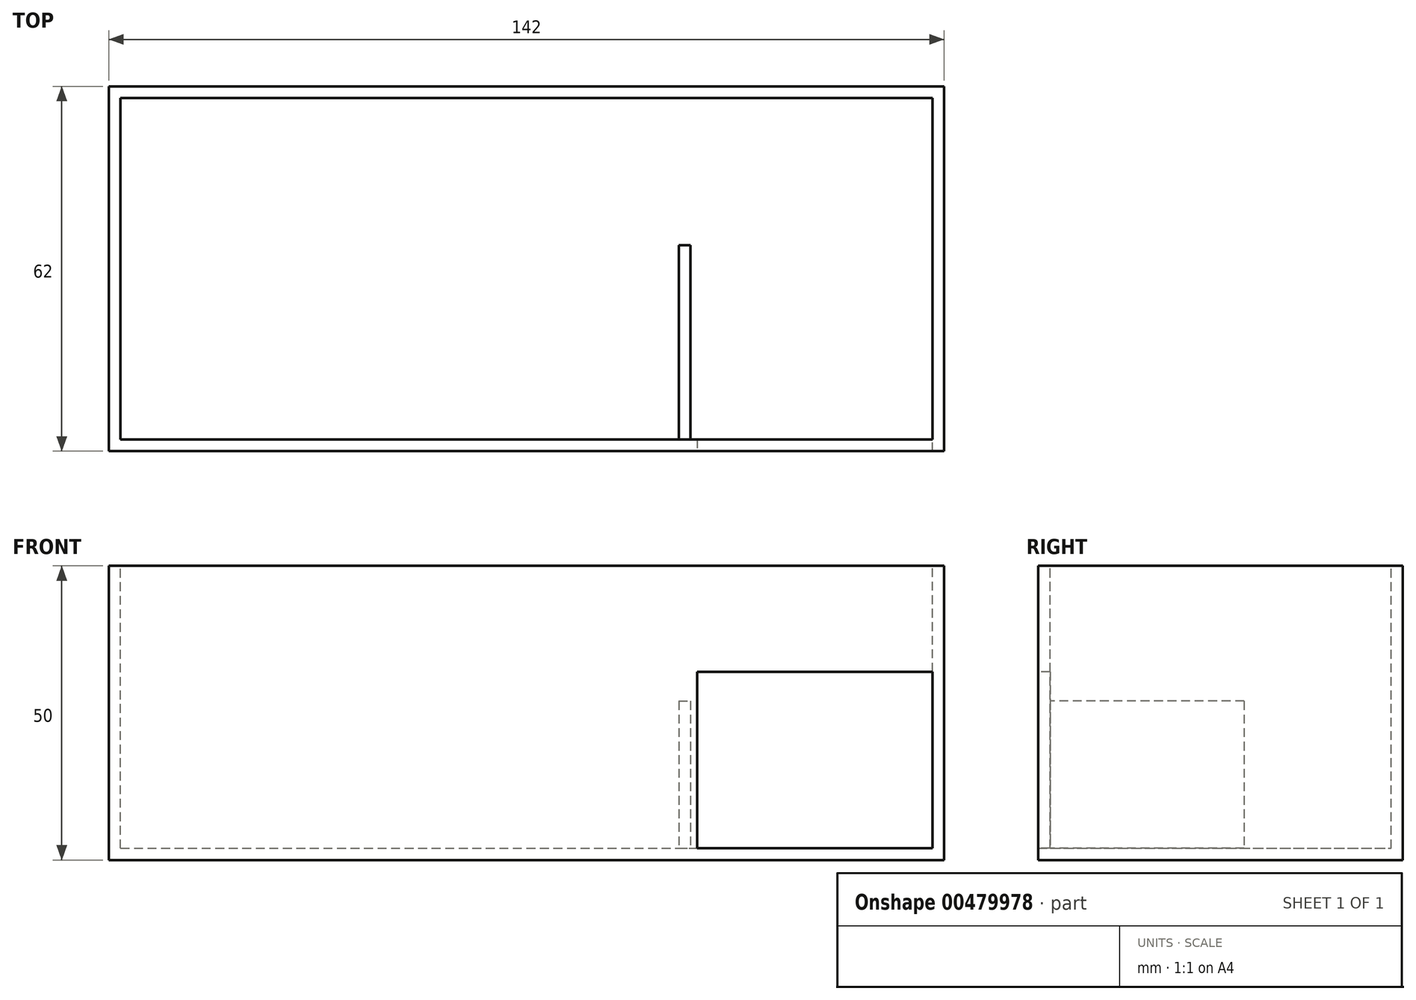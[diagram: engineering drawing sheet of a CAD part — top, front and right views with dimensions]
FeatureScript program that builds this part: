
annotation { "Feature Type Name" : "Feature", "Feature Type Description" : "" }
export const myFeature = defineFeature(function(context is Context, id is Id, definition is map)
    precondition{}
    {
        {
            var Q0;
            Q0=qCreatedBy(makeId("Top.planeOp"),FACE);
            var sketch = newSketch(context, id + "F0", { "sketchPlane" : qUnion([Q0])});
            skLineSegment(sketch, "E0.bottom", {"start": v(-36.08, 27.4) * mm, "end": v(105.92, 27.4) * mm});
            skLineSegment(sketch, "E0.top", {"start": v(-36.08, -34.6) * mm, "end": v(105.92, -34.6) * mm});
            skLineSegment(sketch, "E0.left", {"start": v(-36.08, 27.4) * mm, "end": v(-36.08, -34.6) * mm});
            skLineSegment(sketch, "E0.right", {"start": v(105.92, 27.4) * mm, "end": v(105.92, -34.6) * mm});
            skSolve(sketch);
        }
        {
            var Q0;
            Q0 = qSketchRegion(id + "F0", true);
            var Q1;
            Q1 = qSketchRegion(id + "F5", true);
            extrude(context, id + "F1", {"entities" : qUnion([Q0, Q1]), "depth" : 50 * mm});
        }
        {
            var Q0;
            Q0=makeQuery(id+"F1.opExtrude","CAP_FACE",FACE,{"disambiguationData":[OSD([sQuery(id+"F0.wireOp",EDGE,"E0.bottom"),sQuery(id+"F0.wireOp",EDGE,"E0.top"),sQuery(id+"F0.wireOp",EDGE,"E0.left"),sQuery(id+"F0.wireOp",EDGE,"E0.right")])],"isStart":false});
            var sketch = newSketch(context, id + "F2", { "sketchPlane" : qUnion([Q0])});
            skLineSegment(sketch, "E1.bottom", {"start": v(-34.08, 25.4) * mm, "end": v(103.92, 25.4) * mm});
            skLineSegment(sketch, "E1.top", {"start": v(-34.08, -32.6) * mm, "end": v(103.92, -32.6) * mm});
            skLineSegment(sketch, "E1.left", {"start": v(-34.08, -32.6) * mm, "end": v(-34.08, 25.4) * mm});
            skLineSegment(sketch, "E1.right", {"start": v(103.92, -32.6) * mm, "end": v(103.92, 25.4) * mm});
            skSolve(sketch);
        }
        {
            var Q0;
            Q0 = qSketchRegion(id + "F2", true);
            extrude(context, id + "F3", {"entities" : qUnion([Q0]), "operationType" : NewBodyOperationType.REMOVE, "oppositeDirection" : true, "depth" : 48 * mm});
        }
        {
            var Q0;
            Q0=makeQuery(id+"F3.boolean.opBoolean","COPY",FACE,{"derivedFrom":makeQuery(id+"F3.opExtrude","CAP_FACE",FACE,{"disambiguationData":[OSD([sQuery(id+"F2.wireOp",EDGE,"E1.bottom"),sQuery(id+"F2.wireOp",EDGE,"E1.top"),sQuery(id+"F2.wireOp",EDGE,"E1.left"),sQuery(id+"F2.wireOp",EDGE,"E1.right")])],"isStart":false})});
            var sketch = newSketch(context, id + "F4", { "sketchPlane" : qUnion([Q0])});
            skLineSegment(sketch, "E2", {"start": v(55.92, 25.4) * mm, "end": v(55.92, -32.6) * mm});
            skPoint(sketch, "E2.endSnap0", {"position": v(34.92, -32.6) * mm});
            skSolve(sketch);
        }
        {
            var Q0;
            {var subQ0=sQuery(id+"F2.wireOp",EDGE,"E1.bottom");var subQ1=sQuery(id+"F2.wireOp",EDGE,"E1.top");var subQ2=sQuery(id+"F2.wireOp",EDGE,"E1.left");Q0=makeQuery(id+"FYpbpyhjp7itbWw_2.boolean.opBoolean","SPLIT",FACE,{"disambiguationData":[TD([makeQuery(id+"F3.boolean.opBoolean","COPY",FACE,{"derivedFrom":makeQuery(id+"F3.opExtrude","SWEPT_FACE",FACE,{"disambiguationData":[OSD([subQ2])]})})])],"derivedFrom":makeQuery(id+"F3.boolean.opBoolean","COPY",FACE,{"derivedFrom":makeQuery(id+"F3.opExtrude","CAP_FACE",FACE,{"disambiguationData":[OSD([subQ0,subQ1,subQ2,sQuery(id+"F2.wireOp",EDGE,"E1.right")])],"isStart":false})})});}
            var sketch = newSketch(context, id + "F5", { "sketchPlane" : qUnion([Q0])});
            skSolve(sketch);
        }
        {
            var Q0;
            Q0=makeQuery(id+"F1.opExtrude","SWEPT_FACE",FACE,{"disambiguationData":[OSD([sQuery(id+"F0.wireOp",EDGE,"E0.top")])]});
            var sketch = newSketch(context, id + "F6", { "sketchPlane" : qUnion([Q0])});
            skLineSegment(sketch, "E3.bottom", {"start": v(63.92, 32) * mm, "end": v(103.92, 32) * mm});
            skLineSegment(sketch, "E3.top", {"start": v(63.92, 2) * mm, "end": v(103.92, 2) * mm});
            skLineSegment(sketch, "E3.left", {"start": v(63.92, 32) * mm, "end": v(63.92, 2) * mm});
            skLineSegment(sketch, "E3.right", {"start": v(103.92, 32) * mm, "end": v(103.92, 2) * mm});
            skSolve(sketch);
        }
        {
            var Q0;
            Q0 = qSketchRegion(id + "F6", true);
            extrude(context, id + "F7", {"entities" : qUnion([Q0]), "operationType" : NewBodyOperationType.REMOVE, "oppositeDirection" : true, "depth" : 2 * mm});
        }
        {
            var Q0;
            {var subQ0=sQuery(id+"F4.wireOp",EDGE,"E2");Q0=makeQuery(id+"F4.imprint","IMPRINT",FACE,{"disambiguationData":[TD([[makeQuery(id+"F4.imprint","IMPRINT",EDGE,{"derivedFrom":subQ0}),1.0]])]});}
            var sketch = newSketch(context, id + "F8", { "sketchPlane" : qUnion([Q0])});
            skLineSegment(sketch, "E4.bottom", {"start": v(60.8, 0.4) * mm, "end": v(62.8, 0.4) * mm});
            skLineSegment(sketch, "E4.top", {"start": v(60.8, -32.6) * mm, "end": v(62.8, -32.6) * mm});
            skLineSegment(sketch, "E4.left", {"start": v(60.8, 0.4) * mm, "end": v(60.8, -32.6) * mm});
            skLineSegment(sketch, "E4.right", {"start": v(62.8, 0.4) * mm, "end": v(62.8, -32.6) * mm});
            skSolve(sketch);
        }
        {
            var Q0;
            Q0 = qSketchRegion(id + "F8", true);
            extrude(context, id + "F9", {"entities" : qUnion([Q0]), "operationType" : NewBodyOperationType.ADD, "depth" : 25 * mm});
        }
    });
